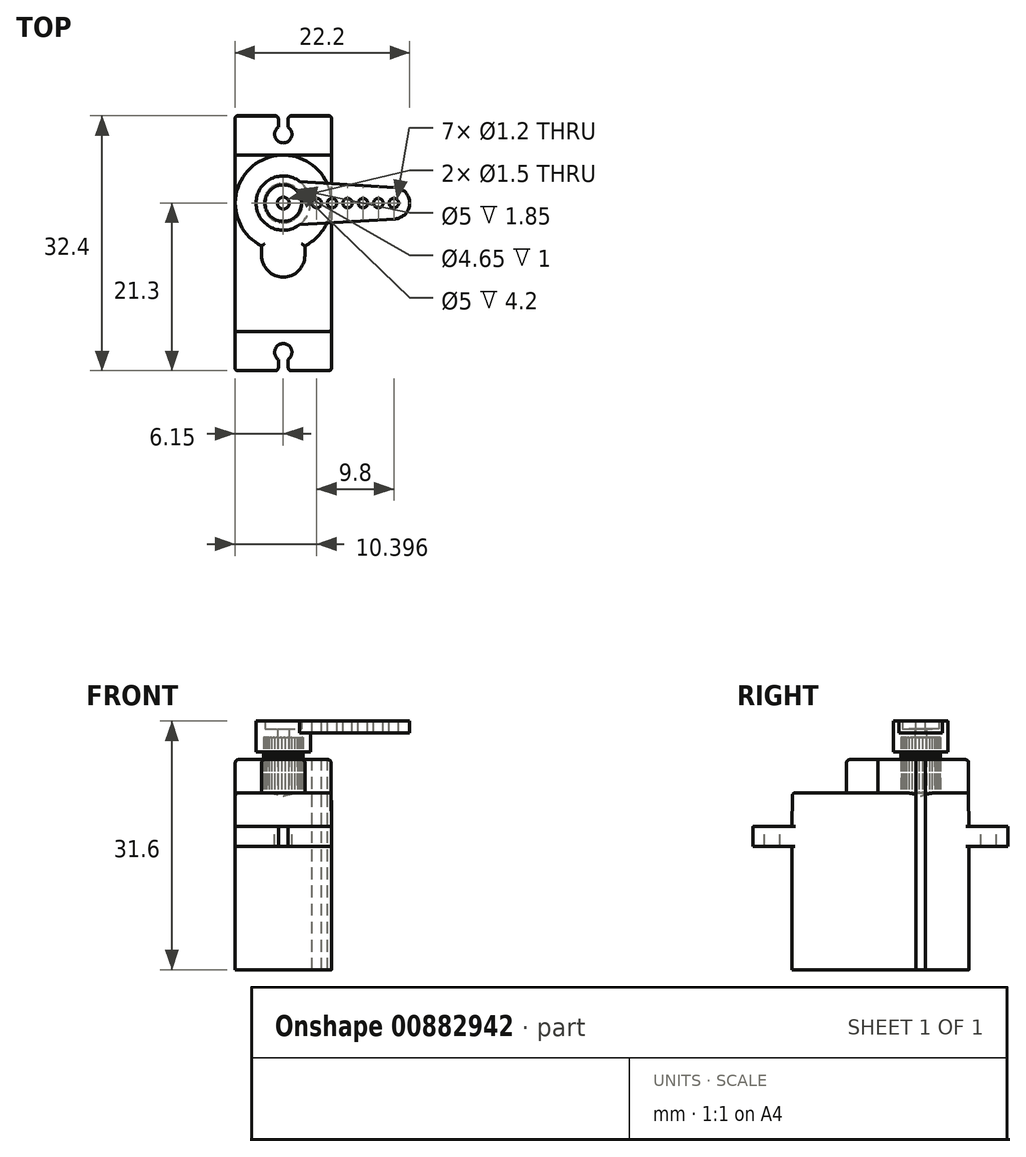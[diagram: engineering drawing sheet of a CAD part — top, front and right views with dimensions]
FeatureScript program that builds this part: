
annotation { "Feature Type Name" : "Feature", "Feature Type Description" : "" }
export const myFeature = defineFeature(function(context is Context, id is Id, definition is map)
    precondition{}
    {
        {
            var Q0;
            Q0=qCreatedBy(makeId("Top.planeOp"),FACE);
            var sketch = newSketch(context, id + "F0", { "sketchPlane" : qUnion([Q0])});
            skLineSegment(sketch, "E0.bottom", {"start": v(6.15, -11.25) * mm, "end": v(-6.15, -11.25) * mm});
            skLineSegment(sketch, "E0.top", {"start": v(6.15, 11.25) * mm, "end": v(-6.15, 11.25) * mm});
            skLineSegment(sketch, "E0.left", {"start": v(6.15, -11.25) * mm, "end": v(6.15, 11.25) * mm});
            skLineSegment(sketch, "E0.right", {"start": v(-6.15, -11.25) * mm, "end": v(-6.15, 11.25) * mm});
            skPoint(sketch, "E0.middle", {"position": v(0, 0) * mm});
            skSolve(sketch);
        }
        {
            var Q0;
            Q0=qSketchRegion(id+"F0",true);
            extrude(context, id + "F1", {"entities" : qUnion([Q0]), "depth" : (22.5 - 15.7) * mm, "hasDraft" : true, "draftAngle" : .5 * degree, "draftPullDirection" : true, "hasSecondDirection" : true, "secondDirectionOppositeDirection" : true, "secondDirectionDepth" : 15.7 * mm});
        }
        {
            var Q0;
            Q0=qCreatedBy(makeId("Top.planeOp"),FACE);
            var sketch = newSketch(context, id + "F2", { "sketchPlane" : qUnion([Q0])});
            skLineSegment(sketch, "E1.bottom", {"start": v(6.15, -16.2) * mm, "end": v(-6.15, -16.2) * mm});
            skLineSegment(sketch, "E1.top", {"start": v(6.15, 16.2) * mm, "end": v(-6.15, 16.2) * mm});
            skLineSegment(sketch, "E1.left", {"start": v(6.15, -16.2) * mm, "end": v(6.15, 16.2) * mm});
            skLineSegment(sketch, "E1.right", {"start": v(-6.15, -16.2) * mm, "end": v(-6.15, 16.2) * mm});
            skPoint(sketch, "E1.middle", {"position": v(0, 0) * mm});
            skSolve(sketch);
        }
        {
            var Q0;
            Q0=qSketchRegion(id+"F2",true);
            extrude(context, id + "F3", {"entities" : qUnion([Q0]), "operationType" : NewBodyOperationType.ADD, "depth" : 2.5 * mm, "hasDraft" : true, "draftAngle" : .5 * degree, "draftPullDirection" : true});
        }
        {
            var Q0;
            {var subQ0=sQuery(id+"F2.wireOp",EDGE,"E1.top");var subQ1=sQuery(id+"F2.wireOp",EDGE,"E1.right");var subQ2=sQuery(id+"F2.wireOp",EDGE,"E1.left");Q0=makeQuery(id+"F3.boolean.opBoolean","SPLIT",FACE,{"disambiguationData":[TD([makeQuery(id+"F1.opExtrude","SWEPT_FACE",FACE,{"disambiguationData":[OSD([sQuery(id+"F0.wireOp",EDGE,"E0.top")])]})])],"derivedFrom":makeQuery(id+"F3.opExtrude","CAP_FACE",FACE,{"disambiguationData":[OSD([sQuery(id+"F2.wireOp",EDGE,"E1.bottom"),subQ0,subQ2,subQ1])],"isStart":false})});}
            var sketch = newSketch(context, id + "F4", { "sketchPlane" : qUnion([Q0])});
            skArc(sketch, "E2", {"start": v(-0.63, 14.76) * mm, "mid": v(0, 12.75) * mm, "end": v(0.63, 14.76) * mm});
            skLineSegment(sketch, "E3", {"start": v(0, 0) * mm, "end": v(0, 13.85) * mm, "construction": true});
            skLineSegment(sketch, "E4", {"start": v(-0.63, 14.76) * mm, "end": v(-0.63, 16.2) * mm});
            skLineSegment(sketch, "E5", {"start": v(-0.62, 16.2) * mm, "end": v(0.62, 16.2) * mm});
            skLineSegment(sketch, "E6", {"start": v(0.62, 16.2) * mm, "end": v(0.62, 14.76) * mm});
            skLineSegment(sketch, "E7", {"start": v(0, 13.85) * mm, "end": v(0, 16.2) * mm, "construction": true});
            skLineSegment(sketch, "E8.MirrorCS", {"start": v(0.62, -16.2) * mm, "end": v(0.62, -14.76) * mm});
            skLineSegment(sketch, "E9.MirrorCS", {"start": v(-0.62, -16.2) * mm, "end": v(0.62, -16.2) * mm});
            skLineSegment(sketch, "E10.MirrorCS", {"start": v(-0.63, -14.76) * mm, "end": v(-0.63, -16.2) * mm});
            skArc(sketch, "E11.MirrorCS", {"start": v(-0.63, -14.76) * mm, "mid": v(0, -12.75) * mm, "end": v(0.63, -14.76) * mm});
            skSolve(sketch);
        }
        {
            var Q0;
            Q0=qSketchRegion(id+"F4",true);
            extrude(context, id + "F5", {"entities" : qUnion([Q0]), "operationType" : NewBodyOperationType.REMOVE, "endBound" : BoundingType.THROUGH_ALL, "oppositeDirection" : true, "depth" : 25 * mm});
        }
        {
            var Q0;
            Q0=makeQuery(id+"F1.*.split.splitOp","SPLIT",EDGE,{"derivedFrom":makeQuery(id+"F1.opExtrude","SWEPT_EDGE",EDGE,{"disambiguationData":[OSD([sQuery(id+"F0.wireOp",EDGE,"E0.bottom"),sQuery(id+"F0.wireOp",EDGE,"E0.left")])]})});
            var Q1;
            Q1=makeQuery(id+"F1.*.split.splitOp","SPLIT",EDGE,{"derivedFrom":makeQuery(id+"F1.opExtrude","SWEPT_EDGE",EDGE,{"disambiguationData":[OSD([sQuery(id+"F0.wireOp",EDGE,"E0.bottom"),sQuery(id+"F0.wireOp",EDGE,"E0.left")])]}),"isFromBackBody":true});
            var Q2;
            Q2=makeQuery(id+"F1.*.split.splitOp","SPLIT",EDGE,{"derivedFrom":makeQuery(id+"F1.opExtrude","SWEPT_EDGE",EDGE,{"disambiguationData":[OSD([sQuery(id+"F0.wireOp",EDGE,"E0.bottom"),sQuery(id+"F0.wireOp",EDGE,"E0.right")])]}),"isFromBackBody":true});
            var Q3;
            Q3=makeQuery(id+"F1.*.split.splitOp","SPLIT",EDGE,{"derivedFrom":makeQuery(id+"F1.opExtrude","SWEPT_EDGE",EDGE,{"disambiguationData":[OSD([sQuery(id+"F0.wireOp",EDGE,"E0.bottom"),sQuery(id+"F0.wireOp",EDGE,"E0.right")])]})});
            var Q4;
            Q4=makeQuery(id+"F1.opExtrude","CAP_FACE",FACE,{"disambiguationData":[OSD([sQuery(id+"F0.wireOp",EDGE,"E0.bottom"),sQuery(id+"F0.wireOp",EDGE,"E0.top"),sQuery(id+"F0.wireOp",EDGE,"E0.left"),sQuery(id+"F0.wireOp",EDGE,"E0.right")])],"isStart":false});
            var Q5;
            Q5=makeQuery(id+"F1.*.split.splitOp","SPLIT",EDGE,{"derivedFrom":makeQuery(id+"F1.opExtrude","SWEPT_EDGE",EDGE,{"disambiguationData":[OSD([sQuery(id+"F0.wireOp",EDGE,"E0.top"),sQuery(id+"F0.wireOp",EDGE,"E0.right")])]})});
            var Q6;
            Q6=makeQuery(id+"F1.*.split.splitOp","SPLIT",EDGE,{"derivedFrom":makeQuery(id+"F1.opExtrude","SWEPT_EDGE",EDGE,{"disambiguationData":[OSD([sQuery(id+"F0.wireOp",EDGE,"E0.top"),sQuery(id+"F0.wireOp",EDGE,"E0.right")])]}),"isFromBackBody":true});
            var Q7;
            Q7=makeQuery(id+"F1.*.split.splitOp","SPLIT",EDGE,{"derivedFrom":makeQuery(id+"F1.opExtrude","SWEPT_EDGE",EDGE,{"disambiguationData":[OSD([sQuery(id+"F0.wireOp",EDGE,"E0.top"),sQuery(id+"F0.wireOp",EDGE,"E0.left")])]}),"isFromBackBody":true});
            var Q8;
            Q8=makeQuery(id+"F1.*.split.splitOp","SPLIT",EDGE,{"derivedFrom":makeQuery(id+"F1.opExtrude","SWEPT_EDGE",EDGE,{"disambiguationData":[OSD([sQuery(id+"F0.wireOp",EDGE,"E0.top"),sQuery(id+"F0.wireOp",EDGE,"E0.left")])]})});
            var Q9;
            Q9=makeQuery(id+"F3.opExtrude","SWEPT_EDGE",EDGE,{"disambiguationData":[OSD([sQuery(id+"F2.wireOp",EDGE,"E1.top"),sQuery(id+"F2.wireOp",EDGE,"E1.left")])]});
            var Q10;
            Q10=makeQuery(id+"F5.boolean.opBoolean","INTERSECT",EDGE,{"derivedFrom":[makeQuery(id+"F3.opExtrude","SWEPT_FACE",FACE,{"disambiguationData":[OSD([sQuery(id+"F2.wireOp",EDGE,"E1.top")])]}),makeQuery(id+"F5.opExtrude","SWEPT_FACE",FACE,{"disambiguationData":[OSD([sQuery(id+"F4.wireOp",EDGE,"E6")])]})]});
            var Q11;
            Q11=makeQuery(id+"F5.boolean.opBoolean","INTERSECT",EDGE,{"derivedFrom":[makeQuery(id+"F3.opExtrude","SWEPT_FACE",FACE,{"disambiguationData":[OSD([sQuery(id+"F2.wireOp",EDGE,"E1.top")])]}),makeQuery(id+"F5.opExtrude","SWEPT_FACE",FACE,{"disambiguationData":[OSD([sQuery(id+"F4.wireOp",EDGE,"E4")])]})]});
            var Q12;
            Q12=makeQuery(id+"F3.opExtrude","SWEPT_EDGE",EDGE,{"disambiguationData":[OSD([sQuery(id+"F2.wireOp",EDGE,"E1.top"),sQuery(id+"F2.wireOp",EDGE,"E1.right")])]});
            var Q13;
            Q13=makeQuery(id+"F3.opExtrude","SWEPT_EDGE",EDGE,{"disambiguationData":[OSD([sQuery(id+"F2.wireOp",EDGE,"E1.bottom"),sQuery(id+"F2.wireOp",EDGE,"E1.right")])]});
            var Q14;
            Q14=makeQuery(id+"F5.boolean.opBoolean","INTERSECT",EDGE,{"derivedFrom":[makeQuery(id+"F3.opExtrude","SWEPT_FACE",FACE,{"disambiguationData":[OSD([sQuery(id+"F2.wireOp",EDGE,"E1.bottom")])]}),makeQuery(id+"F5.opExtrude","SWEPT_FACE",FACE,{"disambiguationData":[OSD([sQuery(id+"F4.wireOp",EDGE,"E10.MirrorCS")])]})]});
            var Q15;
            Q15=makeQuery(id+"F5.boolean.opBoolean","INTERSECT",EDGE,{"derivedFrom":[makeQuery(id+"F3.opExtrude","SWEPT_FACE",FACE,{"disambiguationData":[OSD([sQuery(id+"F2.wireOp",EDGE,"E1.bottom")])]}),makeQuery(id+"F5.opExtrude","SWEPT_FACE",FACE,{"disambiguationData":[OSD([sQuery(id+"F4.wireOp",EDGE,"E8.MirrorCS")])]})]});
            var Q16;
            Q16=makeQuery(id+"F3.opExtrude","SWEPT_EDGE",EDGE,{"disambiguationData":[OSD([sQuery(id+"F2.wireOp",EDGE,"E1.bottom"),sQuery(id+"F2.wireOp",EDGE,"E1.left")])]});
            fillet(context, id + "F6", {"entities" : qUnion([Q0, Q1, Q2, Q3, Q4, Q5, Q6, Q7, Q8, Q9, Q10, Q11, Q12, Q13, Q14, Q15, Q16]), "radius" : .4 * mm, "tangentPropagation" : true, "allowEdgeOverflow" : false});
        }
        {
            var Q0;
            Q0=makeQuery(id+"F1.opExtrude","CAP_FACE",FACE,{"disambiguationData":[OSD([sQuery(id+"F0.wireOp",EDGE,"E0.bottom"),sQuery(id+"F0.wireOp",EDGE,"E0.top"),sQuery(id+"F0.wireOp",EDGE,"E0.left"),sQuery(id+"F0.wireOp",EDGE,"E0.right")])],"isStart":false});
            var sketch = newSketch(context, id + "F7", { "sketchPlane" : qUnion([Q0])});
            skArc(sketch, "E12", {"start": v(2.75, -0.34) * mm, "mid": v(0, 11.2) * mm, "end": v(-2.75, -0.34) * mm});
            skLineSegment(sketch, "E13", {"start": v(-2.75, -0.34) * mm, "end": v(-2.75, -1.56) * mm});
            skLineSegment(sketch, "E14", {"start": v(2.75, -0.34) * mm, "end": v(2.75, -1.56) * mm});
            skArc(sketch, "E15", {"start": v(-2.75, -1.56) * mm, "mid": v(0, -4.3) * mm, "end": v(2.75, -1.56) * mm});
            skCircle(sketch, "E16", {"center": v(0, 5.1) * mm, "radius": 2.5 * mm});
            skSolve(sketch);
        }
        {
            var Q0;
            Q0=qSketchRegion(id+"F7",true);
            extrude(context, id + "F8", {"entities" : qUnion([Q0]), "operationType" : NewBodyOperationType.ADD, "depth" : 4.2 * mm, "hasSecondDirection" : true, "secondDirectionBound" : BoundingType.UP_TO_NEXT, "secondDirectionOppositeDirection" : true, "secondDirectionDepth" : 25 * mm});
        }
        {
            var Q0;
            Q0=makeQuery(id+"F8.opExtrude","CAP_EDGE",EDGE,{"disambiguationData":[OSD([sQuery(id+"F7.wireOp",EDGE,"E12")])],"isStart":false});
            var Q1;
            Q1=makeQuery(id+"F8.opExtrude","CAP_EDGE",EDGE,{"disambiguationData":[OSD([sQuery(id+"F7.wireOp",EDGE,"E14")])],"isStart":false});
            var Q2;
            Q2=makeQuery(id+"F8.opExtrude","CAP_EDGE",EDGE,{"disambiguationData":[OSD([sQuery(id+"F7.wireOp",EDGE,"E15")])],"isStart":false});
            var Q3;
            Q3=makeQuery(id+"F8.opExtrude","CAP_EDGE",EDGE,{"disambiguationData":[OSD([sQuery(id+"F7.wireOp",EDGE,"E13")])],"isStart":false});
            fillet(context, id + "F9", {"entities" : qUnion([Q0, Q1, Q2, Q3]), "radius" : .4 * mm, "tangentPropagation" : true, "allowEdgeOverflow" : false});
        }
        {
            var Q0;
            Q0=makeQuery(id+"F8.opExtrude","CAP_FACE",FACE,{"disambiguationData":[OSD([sQuery(id+"F7.wireOp",EDGE,"E12"),sQuery(id+"F7.wireOp",EDGE,"E13"),sQuery(id+"F7.wireOp",EDGE,"E14"),sQuery(id+"F7.wireOp",EDGE,"E15"),sQuery(id+"F7.wireOp",EDGE,"E16")])],"isStart":false});
            var sketch = newSketch(context, id + "F10", { "sketchPlane" : qUnion([Q0])});
            skCircle(sketch, "E17", {"center": v(0, 5.1) * mm, "radius": 2.3 * mm, "construction": true});
            skLineSegment(sketch, "E18", {"start": v(-0.23, 7.39) * mm, "end": v(-0.06, 7.57) * mm});
            skLineSegment(sketch, "E19", {"start": v(0.23, 7.39) * mm, "end": v(0.06, 7.57) * mm});
            skArc(sketch, "E20", {"start": v(0.06, 7.57) * mm, "mid": v(0, 7.6) * mm, "end": v(-0.06, 7.57) * mm});
            skLineSegment(sketch, "E21", {"start": v(-0.23, 7.39) * mm, "end": v(0, 5.1) * mm, "construction": true});
            skLineSegment(sketch, "E22", {"start": v(0.23, 7.39) * mm, "end": v(0, 5.1) * mm, "construction": true});
            skLineSegment(sketch, "E23.1.0", {"start": v(-0.67, 7.3) * mm, "end": v(-0.54, 7.51) * mm});
            skArc(sketch, "E23.1.1", {"start": v(-0.42, 7.54) * mm, "mid": v(-0.49, 7.55) * mm, "end": v(-0.54, 7.51) * mm});
            skLineSegment(sketch, "E23.1.2", {"start": v(-0.23, 7.39) * mm, "end": v(-0.42, 7.54) * mm});
            skLineSegment(sketch, "E23.2.0", {"start": v(-1.08, 7.13) * mm, "end": v(-1, 7.36) * mm});
            skArc(sketch, "E23.2.1", {"start": v(-0.9, 7.4) * mm, "mid": v(-0.96, 7.4) * mm, "end": v(-1, 7.36) * mm});
            skLineSegment(sketch, "E23.2.2", {"start": v(-0.67, 7.3) * mm, "end": v(-0.9, 7.4) * mm});
            skLineSegment(sketch, "E23.3.0", {"start": v(-1.46, 6.88) * mm, "end": v(-1.42, 7.12) * mm});
            skArc(sketch, "E23.3.1", {"start": v(-1.32, 7.19) * mm, "mid": v(-1.39, 7.18) * mm, "end": v(-1.42, 7.12) * mm});
            skLineSegment(sketch, "E23.3.2", {"start": v(-1.08, 7.13) * mm, "end": v(-1.32, 7.19) * mm});
            skLineSegment(sketch, "E23.4.0", {"start": v(-1.78, 6.56) * mm, "end": v(-1.8, 6.8) * mm});
            skArc(sketch, "E23.4.1", {"start": v(-1.7, 6.9) * mm, "mid": v(-1.77, 6.87) * mm, "end": v(-1.8, 6.8) * mm});
            skLineSegment(sketch, "E23.4.2", {"start": v(-1.46, 6.88) * mm, "end": v(-1.7, 6.9) * mm});
            skLineSegment(sketch, "E23.5.0", {"start": v(-2.03, 6.18) * mm, "end": v(-2.09, 6.42) * mm});
            skArc(sketch, "E23.5.1", {"start": v(-2.02, 6.52) * mm, "mid": v(-2.08, 6.49) * mm, "end": v(-2.09, 6.42) * mm});
            skLineSegment(sketch, "E23.5.2", {"start": v(-1.78, 6.56) * mm, "end": v(-2.02, 6.52) * mm});
            skLineSegment(sketch, "E23.6.0", {"start": v(-2.2, 5.77) * mm, "end": v(-2.3, 6) * mm});
            skArc(sketch, "E23.6.1", {"start": v(-2.26, 6.1) * mm, "mid": v(-2.3, 6.06) * mm, "end": v(-2.3, 6) * mm});
            skLineSegment(sketch, "E23.6.2", {"start": v(-2.03, 6.18) * mm, "end": v(-2.26, 6.1) * mm});
            skLineSegment(sketch, "E23.7.0", {"start": v(-2.29, 5.33) * mm, "end": v(-2.44, 5.52) * mm});
            skArc(sketch, "E23.7.1", {"start": v(-2.41, 5.64) * mm, "mid": v(-2.45, 5.59) * mm, "end": v(-2.44, 5.52) * mm});
            skLineSegment(sketch, "E23.7.2", {"start": v(-2.2, 5.77) * mm, "end": v(-2.41, 5.64) * mm});
            skLineSegment(sketch, "E23.8.0", {"start": v(-2.29, 4.87) * mm, "end": v(-2.47, 5.04) * mm});
            skArc(sketch, "E23.8.1", {"start": v(-2.47, 5.16) * mm, "mid": v(-2.5, 5.1) * mm, "end": v(-2.47, 5.04) * mm});
            skLineSegment(sketch, "E23.8.2", {"start": v(-2.29, 5.33) * mm, "end": v(-2.47, 5.16) * mm});
            skLineSegment(sketch, "E23.9.0", {"start": v(-2.2, 4.43) * mm, "end": v(-2.41, 4.56) * mm});
            skArc(sketch, "E23.9.1", {"start": v(-2.44, 4.68) * mm, "mid": v(-2.45, 4.61) * mm, "end": v(-2.41, 4.56) * mm});
            skLineSegment(sketch, "E23.9.2", {"start": v(-2.29, 4.87) * mm, "end": v(-2.44, 4.68) * mm});
            skLineSegment(sketch, "E23.10.0", {"start": v(-2.03, 4.02) * mm, "end": v(-2.26, 4.1) * mm});
            skArc(sketch, "E23.10.1", {"start": v(-2.3, 4.2) * mm, "mid": v(-2.3, 4.14) * mm, "end": v(-2.26, 4.1) * mm});
            skLineSegment(sketch, "E23.10.2", {"start": v(-2.2, 4.43) * mm, "end": v(-2.3, 4.2) * mm});
            skLineSegment(sketch, "E23.11.0", {"start": v(-1.78, 3.64) * mm, "end": v(-2.02, 3.68) * mm});
            skArc(sketch, "E23.11.1", {"start": v(-2.09, 3.78) * mm, "mid": v(-2.08, 3.71) * mm, "end": v(-2.02, 3.68) * mm});
            skLineSegment(sketch, "E23.11.2", {"start": v(-2.03, 4.02) * mm, "end": v(-2.09, 3.78) * mm});
            skLineSegment(sketch, "E23.12.0", {"start": v(-1.46, 3.32) * mm, "end": v(-1.7, 3.3) * mm});
            skArc(sketch, "E23.12.1", {"start": v(-1.8, 3.4) * mm, "mid": v(-1.77, 3.33) * mm, "end": v(-1.7, 3.3) * mm});
            skLineSegment(sketch, "E23.12.2", {"start": v(-1.78, 3.64) * mm, "end": v(-1.8, 3.4) * mm});
            skLineSegment(sketch, "E23.13.0", {"start": v(-1.08, 3.07) * mm, "end": v(-1.32, 3.01) * mm});
            skArc(sketch, "E23.13.1", {"start": v(-1.42, 3.08) * mm, "mid": v(-1.39, 3.02) * mm, "end": v(-1.32, 3.01) * mm});
            skLineSegment(sketch, "E23.13.2", {"start": v(-1.46, 3.32) * mm, "end": v(-1.42, 3.08) * mm});
            skLineSegment(sketch, "E23.14.0", {"start": v(-0.67, 2.9) * mm, "end": v(-0.9, 2.8) * mm});
            skArc(sketch, "E23.14.1", {"start": v(-1, 2.84) * mm, "mid": v(-0.96, 2.8) * mm, "end": v(-0.9, 2.8) * mm});
            skLineSegment(sketch, "E23.14.2", {"start": v(-1.08, 3.07) * mm, "end": v(-1, 2.84) * mm});
            skLineSegment(sketch, "E23.15.0", {"start": v(-0.23, 2.81) * mm, "end": v(-0.42, 2.66) * mm});
            skArc(sketch, "E23.15.1", {"start": v(-0.54, 2.69) * mm, "mid": v(-0.49, 2.65) * mm, "end": v(-0.42, 2.66) * mm});
            skLineSegment(sketch, "E23.15.2", {"start": v(-0.67, 2.9) * mm, "end": v(-0.54, 2.69) * mm});
            skLineSegment(sketch, "E23.16.0", {"start": v(0.23, 2.81) * mm, "end": v(0.06, 2.63) * mm});
            skArc(sketch, "E23.16.1", {"start": v(-0.06, 2.63) * mm, "mid": v(0, 2.6) * mm, "end": v(0.06, 2.63) * mm});
            skLineSegment(sketch, "E23.16.2", {"start": v(-0.23, 2.81) * mm, "end": v(-0.06, 2.63) * mm});
            skLineSegment(sketch, "E23.17.0", {"start": v(0.67, 2.9) * mm, "end": v(0.54, 2.69) * mm});
            skArc(sketch, "E23.17.1", {"start": v(0.42, 2.66) * mm, "mid": v(0.49, 2.65) * mm, "end": v(0.54, 2.69) * mm});
            skLineSegment(sketch, "E23.17.2", {"start": v(0.23, 2.81) * mm, "end": v(0.42, 2.66) * mm});
            skLineSegment(sketch, "E23.18.0", {"start": v(1.08, 3.07) * mm, "end": v(1, 2.84) * mm});
            skArc(sketch, "E23.18.1", {"start": v(0.9, 2.8) * mm, "mid": v(0.96, 2.8) * mm, "end": v(1, 2.84) * mm});
            skLineSegment(sketch, "E23.18.2", {"start": v(0.67, 2.9) * mm, "end": v(0.9, 2.8) * mm});
            skLineSegment(sketch, "E23.19.0", {"start": v(1.46, 3.32) * mm, "end": v(1.42, 3.08) * mm});
            skArc(sketch, "E23.19.1", {"start": v(1.32, 3.01) * mm, "mid": v(1.39, 3.02) * mm, "end": v(1.42, 3.08) * mm});
            skLineSegment(sketch, "E23.19.2", {"start": v(1.08, 3.07) * mm, "end": v(1.32, 3.01) * mm});
            skLineSegment(sketch, "E23.20.0", {"start": v(1.78, 3.64) * mm, "end": v(1.8, 3.4) * mm});
            skArc(sketch, "E23.20.1", {"start": v(1.7, 3.3) * mm, "mid": v(1.77, 3.33) * mm, "end": v(1.8, 3.4) * mm});
            skLineSegment(sketch, "E23.20.2", {"start": v(1.46, 3.32) * mm, "end": v(1.7, 3.3) * mm});
            skLineSegment(sketch, "E23.21.0", {"start": v(2.03, 4.02) * mm, "end": v(2.09, 3.78) * mm});
            skArc(sketch, "E23.21.1", {"start": v(2.02, 3.68) * mm, "mid": v(2.08, 3.71) * mm, "end": v(2.09, 3.78) * mm});
            skLineSegment(sketch, "E23.21.2", {"start": v(1.78, 3.64) * mm, "end": v(2.02, 3.68) * mm});
            skLineSegment(sketch, "E23.22.0", {"start": v(2.2, 4.43) * mm, "end": v(2.3, 4.2) * mm});
            skArc(sketch, "E23.22.1", {"start": v(2.26, 4.1) * mm, "mid": v(2.3, 4.14) * mm, "end": v(2.3, 4.2) * mm});
            skLineSegment(sketch, "E23.22.2", {"start": v(2.03, 4.02) * mm, "end": v(2.26, 4.1) * mm});
            skLineSegment(sketch, "E23.23.0", {"start": v(2.29, 4.87) * mm, "end": v(2.44, 4.68) * mm});
            skArc(sketch, "E23.23.1", {"start": v(2.41, 4.56) * mm, "mid": v(2.45, 4.61) * mm, "end": v(2.44, 4.68) * mm});
            skLineSegment(sketch, "E23.23.2", {"start": v(2.2, 4.43) * mm, "end": v(2.41, 4.56) * mm});
            skLineSegment(sketch, "E23.24.0", {"start": v(2.29, 5.33) * mm, "end": v(2.47, 5.16) * mm});
            skArc(sketch, "E23.24.1", {"start": v(2.47, 5.04) * mm, "mid": v(2.5, 5.1) * mm, "end": v(2.47, 5.16) * mm});
            skLineSegment(sketch, "E23.24.2", {"start": v(2.29, 4.87) * mm, "end": v(2.47, 5.04) * mm});
            skLineSegment(sketch, "E23.25.0", {"start": v(2.2, 5.77) * mm, "end": v(2.41, 5.64) * mm});
            skArc(sketch, "E23.25.1", {"start": v(2.44, 5.52) * mm, "mid": v(2.45, 5.59) * mm, "end": v(2.41, 5.64) * mm});
            skLineSegment(sketch, "E23.25.2", {"start": v(2.29, 5.33) * mm, "end": v(2.44, 5.52) * mm});
            skLineSegment(sketch, "E23.26.0", {"start": v(2.03, 6.18) * mm, "end": v(2.26, 6.1) * mm});
            skArc(sketch, "E23.26.1", {"start": v(2.3, 6) * mm, "mid": v(2.3, 6.06) * mm, "end": v(2.26, 6.1) * mm});
            skLineSegment(sketch, "E23.26.2", {"start": v(2.2, 5.77) * mm, "end": v(2.3, 6) * mm});
            skLineSegment(sketch, "E23.27.0", {"start": v(1.78, 6.56) * mm, "end": v(2.02, 6.52) * mm});
            skArc(sketch, "E23.27.1", {"start": v(2.09, 6.42) * mm, "mid": v(2.08, 6.49) * mm, "end": v(2.02, 6.52) * mm});
            skLineSegment(sketch, "E23.27.2", {"start": v(2.03, 6.18) * mm, "end": v(2.09, 6.42) * mm});
            skLineSegment(sketch, "E23.28.0", {"start": v(1.46, 6.88) * mm, "end": v(1.7, 6.9) * mm});
            skArc(sketch, "E23.28.1", {"start": v(1.8, 6.8) * mm, "mid": v(1.77, 6.87) * mm, "end": v(1.7, 6.9) * mm});
            skLineSegment(sketch, "E23.28.2", {"start": v(1.78, 6.56) * mm, "end": v(1.8, 6.8) * mm});
            skLineSegment(sketch, "E23.29.0", {"start": v(1.08, 7.13) * mm, "end": v(1.32, 7.19) * mm});
            skArc(sketch, "E23.29.1", {"start": v(1.42, 7.12) * mm, "mid": v(1.39, 7.18) * mm, "end": v(1.32, 7.19) * mm});
            skLineSegment(sketch, "E23.29.2", {"start": v(1.46, 6.88) * mm, "end": v(1.42, 7.12) * mm});
            skLineSegment(sketch, "E23.30.0", {"start": v(0.67, 7.3) * mm, "end": v(0.9, 7.4) * mm});
            skArc(sketch, "E23.30.1", {"start": v(1, 7.36) * mm, "mid": v(0.96, 7.4) * mm, "end": v(0.9, 7.4) * mm});
            skLineSegment(sketch, "E23.30.2", {"start": v(1.08, 7.13) * mm, "end": v(1, 7.36) * mm});
            skLineSegment(sketch, "E23.31.0", {"start": v(0.23, 7.39) * mm, "end": v(0.42, 7.54) * mm});
            skArc(sketch, "E23.31.1", {"start": v(0.54, 7.51) * mm, "mid": v(0.49, 7.55) * mm, "end": v(0.42, 7.54) * mm});
            skLineSegment(sketch, "E23.31.2", {"start": v(0.67, 7.3) * mm, "end": v(0.54, 7.51) * mm});
            skCircle(sketch, "E24", {"center": v(0, 5.1) * mm, "radius": 0.75 * mm});
            skSolve(sketch);
        }
        {
            var Q0;
            Q0=qSketchRegion(id+"F10",true);
            extrude(context, id + "F11", {"entities" : qUnion([Q0]), "depth" : 2.85 * mm, "hasSecondDirection" : true, "secondDirectionBound" : BoundingType.UP_TO_NEXT, "secondDirectionOppositeDirection" : true, "secondDirectionDepth" : 25 * mm});
        }
        {
            var Q0;
            Q0=qCreatedBy(makeId("Right.planeOp"),FACE);
            var sketch = newSketch(context, id + "F12", { "sketchPlane" : qUnion([Q0])});
            skLineSegment(sketch, "E25.0", {"start": v(4.35, 13.85) * mm, "end": v(5.85, 13.85) * mm, "construction": true});
            skLineSegment(sketch, "E26", {"start": v(5.85, 13.85) * mm, "end": v(7.6, 13.85) * mm});
            skLineSegment(sketch, "E27", {"start": v(7.6, 13.85) * mm, "end": v(7.6, 12) * mm});
            skLineSegment(sketch, "E28", {"start": v(7.6, 12) * mm, "end": v(8.55, 12) * mm});
            skLineSegment(sketch, "E29", {"start": v(8.55, 12) * mm, "end": v(8.55, 15.9) * mm});
            skLineSegment(sketch, "E30", {"start": v(8.55, 15.9) * mm, "end": v(7.43, 15.9) * mm});
            skLineSegment(sketch, "E31", {"start": v(7.43, 15.9) * mm, "end": v(7.43, 14.9) * mm});
            skLineSegment(sketch, "E32", {"start": v(7.43, 14.9) * mm, "end": v(5.85, 14.9) * mm});
            skLineSegment(sketch, "E33", {"start": v(5.85, 14.9) * mm, "end": v(5.85, 13.85) * mm});
            skLineSegment(sketch, "E34", {"start": v(5.1, 13.85) * mm, "end": v(5.1, 16.3) * mm, "construction": true});
            skLineSegment(sketch, "E35.0", {"start": v(2.6, 11) * mm, "end": v(7.6, 11) * mm, "construction": true});
            skSolve(sketch);
        }
        {
            var Q0;
            Q0=qSketchRegion(id+"F12",true);
            var Q1;
            Q1=sQuery(id+"F12.wireOp",EDGE,"E34");
            revolve(context, id + "F13", {"entities" : qUnion([Q0]), "axis" : qUnion([Q1]), "revolveType" : RevolveType.FULL});
        }
        {
            var Q0;
            Q0=makeQuery(id+"F13.opRevolve","SWEPT_FACE",FACE,{"disambiguationData":[OSD([sQuery(id+"F12.wireOp",EDGE,"E30")])]});
            var sketch = newSketch(context, id + "F14", { "sketchPlane" : qUnion([Q0])});
            skLineSegment(sketch, "E36", {"start": v(2.08, 2.35) * mm, "end": v(14.17, 3.1) * mm});
            skLineSegment(sketch, "E37", {"start": v(2.08, 7.85) * mm, "end": v(14.17, 7.1) * mm});
            skLineSegment(sketch, "E38", {"start": v(0, 5.1) * mm, "end": v(14.05, 5.1) * mm, "construction": true});
            skArc(sketch, "E39", {"start": v(14.17, 3.1) * mm, "mid": v(16.05, 5.1) * mm, "end": v(14.17, 7.1) * mm});
            skArc(sketch, "E40.0", {"start": v(2.08, 2.35) * mm, "mid": v(3.45, 5.1) * mm, "end": v(2.08, 7.85) * mm});
            skSolve(sketch);
        }
        {
            var Q0;
            Q0=qSketchRegion(id+"F14",true);
            extrude(context, id + "F15", {"entities" : qUnion([Q0]), "operationType" : NewBodyOperationType.ADD, "oppositeDirection" : true, "depth" : 1.5 * mm});
        }
        {
            var Q0;
            Q0=makeQuery(id+"F15.boolean.opBoolean","MERGE",FACE,{"derivedFrom":[makeQuery(id+"F13.opRevolve","SWEPT_FACE",FACE,{"disambiguationData":[OSD([sQuery(id+"F12.wireOp",EDGE,"E30")])]}),makeQuery(id+"F15.opExtrude","CAP_FACE",FACE,{"disambiguationData":[OSD([sQuery(id+"F14.wireOp",EDGE,"E36"),sQuery(id+"F14.wireOp",EDGE,"E37"),sQuery(id+"F14.wireOp",EDGE,"E39"),sQuery(id+"F14.wireOp",EDGE,"E40.0")])],"isStart":true})]});
            var sketch = newSketch(context, id + "F16", { "sketchPlane" : qUnion([Q0])});
            skCircle(sketch, "E41", {"center": v(14.05, 5.1) * mm, "radius": 0.6 * mm});
            skCircle(sketch, "E42.1.0.0", {"center": v(12.09, 5.1) * mm, "radius": 0.6 * mm});
            skCircle(sketch, "E42.2.0.0", {"center": v(10.13, 5.1) * mm, "radius": 0.6 * mm});
            skCircle(sketch, "E42.3.0.0", {"center": v(8.17, 5.1) * mm, "radius": 0.6 * mm});
            skCircle(sketch, "E42.4.0.0", {"center": v(6.2, 5.1) * mm, "radius": 0.6 * mm});
            skCircle(sketch, "E42.5.0.0", {"center": v(4.25, 5.1) * mm, "radius": 0.6 * mm});
            skLineSegment(sketch, "E42.direction1", {"start": v(14.05, 5.1) * mm, "end": v(12.09, 5.1) * mm, "construction": true});
            skSolve(sketch);
        }
        {
            var Q0;
            Q0=qSketchRegion(id+"F16",true);
            extrude(context, id + "F17", {"entities" : qUnion([Q0]), "operationType" : NewBodyOperationType.REMOVE, "endBound" : BoundingType.THROUGH_ALL, "oppositeDirection" : true, "depth" : 25 * mm});
        }
    });
